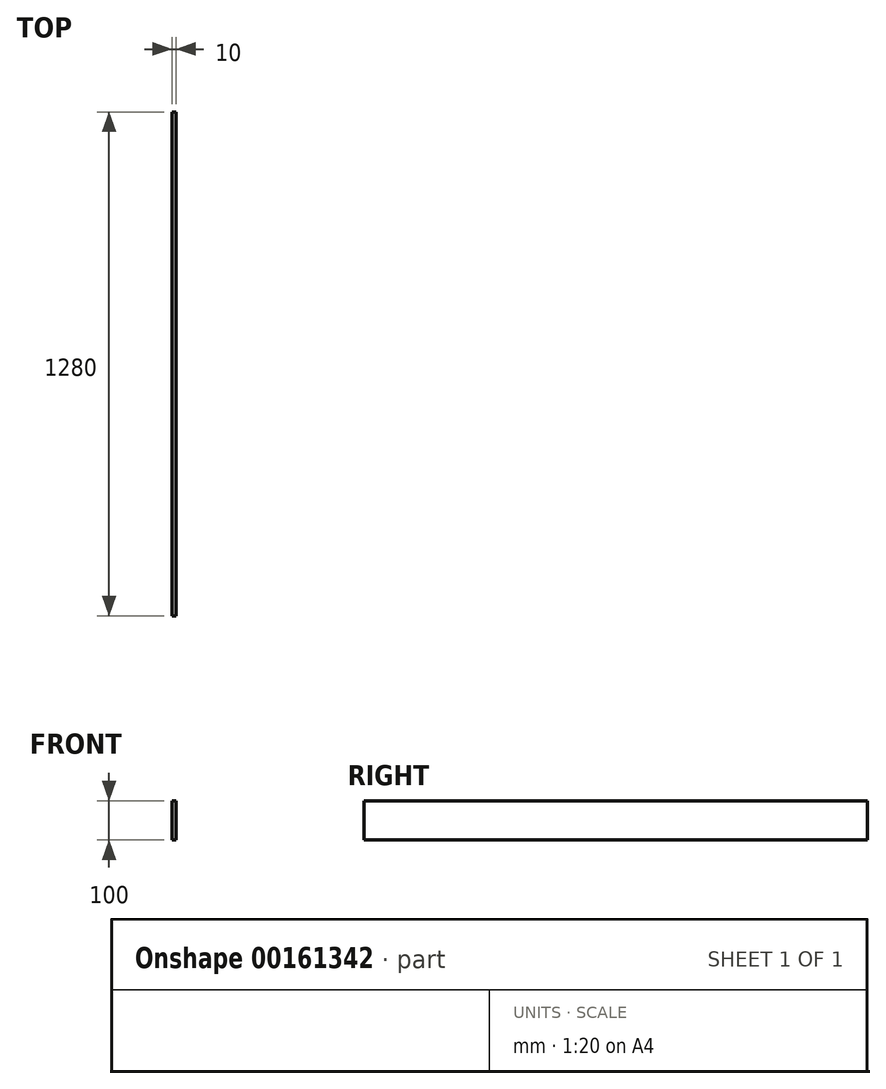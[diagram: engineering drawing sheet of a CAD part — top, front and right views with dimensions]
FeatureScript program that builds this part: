
annotation { "Feature Type Name" : "Feature", "Feature Type Description" : "" }
export const myFeature = defineFeature(function(context is Context, id is Id, definition is map)
    precondition{}
    {
        {
            var Q0;
            Q0=qCreatedBy(makeId("Front.planeOp"),FACE);
            var sketch = newSketch(context, id + "F0", { "sketchPlane" : qUnion([Q0])});
            skLineSegment(sketch, "E0.bottom", {"start": v(0, 0) * mm, "end": v(10, 0) * mm});
            skLineSegment(sketch, "E0.top", {"start": v(0, 100) * mm, "end": v(10, 100) * mm});
            skLineSegment(sketch, "E0.left", {"start": v(0, 0) * mm, "end": v(0, 100) * mm});
            skLineSegment(sketch, "E0.right", {"start": v(10, 0) * mm, "end": v(10, 100) * mm});
            skSolve(sketch);
        }
        {
            var Q0;
            Q0=makeQuery(id+"F0.imprint","IMPRINT",FACE,{"disambiguationData":[TD([[makeQuery(id+"F0.imprint","IMPRINT",EDGE,{"derivedFrom":sQuery(id+"F0.wireOp",EDGE,"epF4zVEX-jh5C-xLuA-YM3R-CBOHCvnoEyUI")}),-1.0]])]});
            var Q1;
            Q1=makeQuery(id+"F0.imprint","IMPRINT",FACE,{"disambiguationData":[TD([[makeQuery(id+"F0.imprint","IMPRINT",EDGE,{"derivedFrom":sQuery(id+"F0.wireOp",EDGE,"E0.bottom")}),1.0]])]});
            extrude(context, id + "F1", {"entities" : qUnion([Q0, Q1]), "depth" : 1280 * mm});
        }
    });
